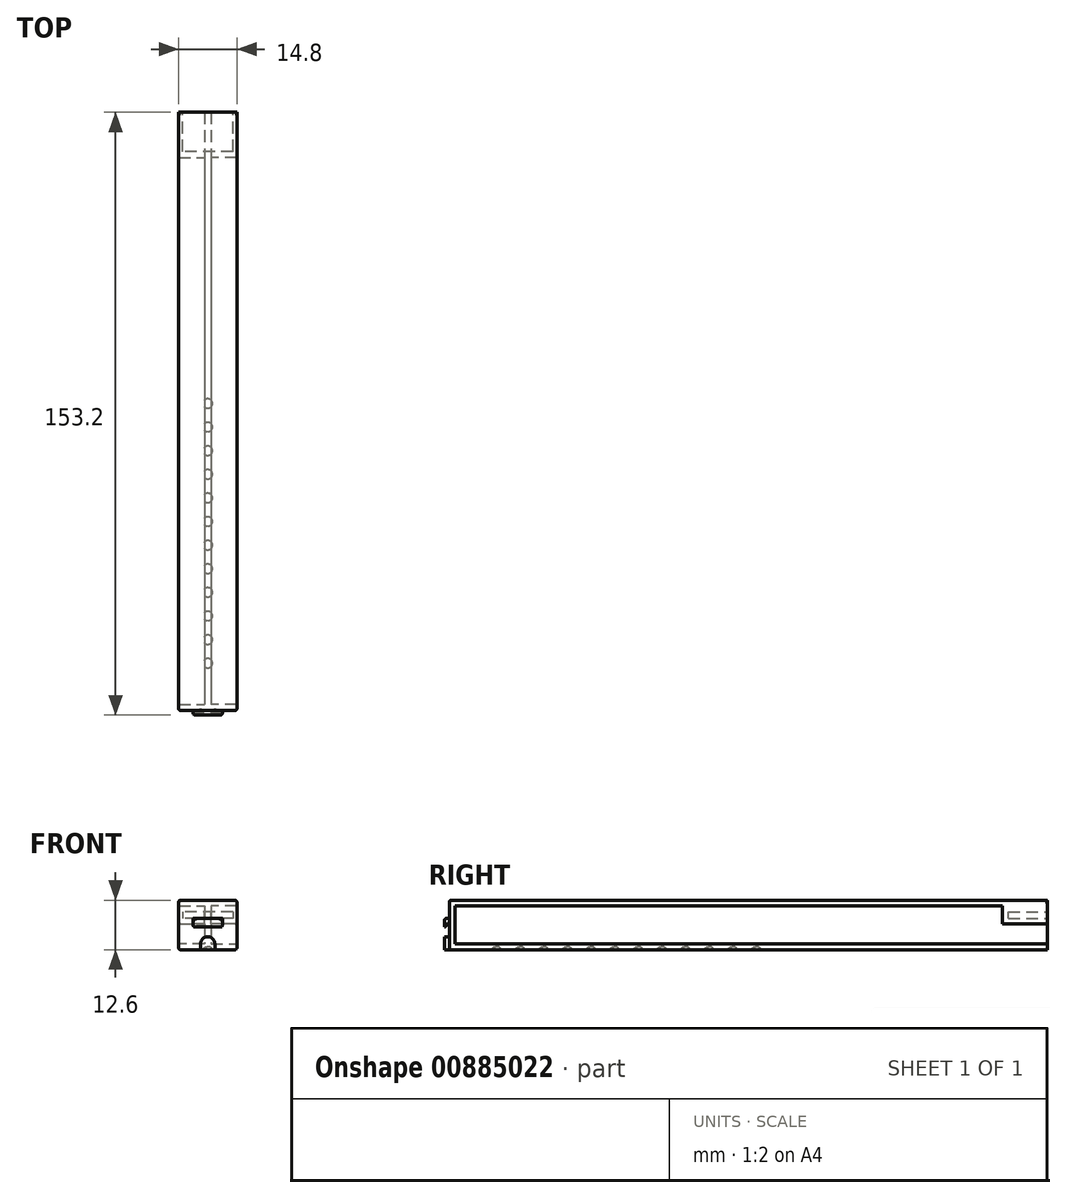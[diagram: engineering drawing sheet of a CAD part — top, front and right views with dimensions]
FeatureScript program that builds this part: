
annotation { "Feature Type Name" : "Feature", "Feature Type Description" : "" }
export const myFeature = defineFeature(function(context is Context, id is Id, definition is map)
    precondition{}
    {
        {
            var Q0;
            Q0=qCreatedBy(makeId("Front.planeOp"),FACE);
            var sketch = newSketch(context, id + "F0", { "sketchPlane" : qUnion([Q0])});
            skLineSegment(sketch, "E0", {"start": v(0, 0) * mm, "end": v(7.4, 0) * mm});
            skLineSegment(sketch, "E1", {"start": v(7.4, 0) * mm, "end": v(7.4, 12.6) * mm, "construction": true});
            skLineSegment(sketch, "E2", {"start": v(7.4, 12.6) * mm, "end": v(0, 12.6) * mm});
            skLineSegment(sketch, "E3", {"start": v(0, 12.6) * mm, "end": v(0, 11.1) * mm});
            skLineSegment(sketch, "E4", {"start": v(0, 11.1) * mm, "end": v(6.6, 11.1) * mm});
            skLineSegment(sketch, "E5", {"start": v(6.6, 11.1) * mm, "end": v(6.6, 1.5) * mm});
            skLineSegment(sketch, "E6", {"start": v(6.6, 1.5) * mm, "end": v(0, 1.5) * mm});
            skLineSegment(sketch, "E7", {"start": v(0, 1.5) * mm, "end": v(0, 0) * mm});
            skLineSegment(sketch, "E8.MirrorCS", {"start": v(7.4, 12.6) * mm, "end": v(14.8, 12.6) * mm});
            skLineSegment(sketch, "E9.MirrorCS", {"start": v(14.8, 12.6) * mm, "end": v(14.8, 11.1) * mm});
            skLineSegment(sketch, "E10.MirrorCS", {"start": v(14.8, 11.1) * mm, "end": v(8.2, 11.1) * mm});
            skLineSegment(sketch, "E11.MirrorCS", {"start": v(8.2, 11.1) * mm, "end": v(8.2, 1.5) * mm});
            skLineSegment(sketch, "E12.MirrorCS", {"start": v(8.2, 1.5) * mm, "end": v(14.8, 1.5) * mm});
            skLineSegment(sketch, "E13.MirrorCS", {"start": v(14.8, 1.5) * mm, "end": v(14.8, 0) * mm});
            skLineSegment(sketch, "E14.MirrorCS", {"start": v(14.8, 0) * mm, "end": v(7.4, 0) * mm});
            skSolve(sketch);
        }
        {
            var Q0;
            Q0=makeQuery(id+"F0.imprint","IMPRINT",FACE,{"disambiguationData":[TD([[makeQuery(id+"F0.imprint","IMPRINT",EDGE,{"derivedFrom":sQuery(id+"F0.wireOp",EDGE,"E0")}),1.0]])]});
            extrude(context, id + "F1", {"entities" : qUnion([Q0]), "oppositeDirection" : true, "depth" : 152 * mm, "offsetDistance" : 25 * mm});
        }
        {
            var Q0;
            Q0=makeQuery(id+"F1.opExtrude","SWEPT_FACE",FACE,{"disambiguationData":[OSD([sQuery(id+"F0.wireOp",EDGE,"E11.MirrorCS")])]});
            var sketch = newSketch(context, id + "F2", { "sketchPlane" : qUnion([Q0])});
            skLineSegment(sketch, "E15.bottom", {"start": v(0, 11.1) * mm, "end": v(1.5, 11.1) * mm});
            skLineSegment(sketch, "E15.top", {"start": v(0, 1.5) * mm, "end": v(1.5, 1.5) * mm});
            skLineSegment(sketch, "E15.left", {"start": v(0, 11.1) * mm, "end": v(0, 1.5) * mm});
            skLineSegment(sketch, "E15.right", {"start": v(1.5, 11.1) * mm, "end": v(1.5, 1.5) * mm});
            skSolve(sketch);
        }
        {
            var Q0;
            Q0=makeQuery(id+"F2.imprint","IMPRINT",FACE,{"disambiguationData":[TD([[makeQuery(id+"F2.imprint","IMPRINT",EDGE,{"derivedFrom":sQuery(id+"F2.wireOp",EDGE,"E15.bottom")}),1.0]])]});
            var Q1;
            Q1=makeQuery(id+"F1.opExtrude","SWEPT_FACE",FACE,{"disambiguationData":[OSD([sQuery(id+"F0.wireOp",EDGE,"E9.MirrorCS")])]});
            extrude(context, id + "F3", {"entities" : qUnion([Q0]), "operationType" : NewBodyOperationType.ADD, "endBound" : BoundingType.UP_TO_SURFACE, "depth" : 25 * mm, "endBoundEntityFace" : qUnion([Q1]), "offsetDistance" : 25 * mm});
        }
        {
            var Q0;
            Q0=makeQuery(id+"F1.opExtrude","SWEPT_FACE",FACE,{"disambiguationData":[OSD([sQuery(id+"F0.wireOp",EDGE,"E5")])]});
            var sketch = newSketch(context, id + "F4", { "sketchPlane" : qUnion([Q0])});
            skLineSegment(sketch, "E16.0", {"start": v(-1.5, 11.1) * mm, "end": v(-1.5, 1.5) * mm});
            skSolve(sketch);
        }
        {
            var Q0;
            {var subQ0=sQuery(id+"F4.wireOp",EDGE,"E16.0");Q0=makeQuery(id+"F4.imprint","IMPRINT",FACE,{"disambiguationData":[TD([[makeQuery(id+"F4.imprint","IMPRINT",EDGE,{"derivedFrom":subQ0}),1.0]])]});}
            var Q1;
            Q1=makeQuery(id+"F1.opExtrude","SWEPT_FACE",FACE,{"disambiguationData":[OSD([sQuery(id+"F0.wireOp",EDGE,"E3")])]});
            extrude(context, id + "F5", {"entities" : qUnion([Q0]), "operationType" : NewBodyOperationType.ADD, "endBound" : BoundingType.UP_TO_SURFACE, "depth" : 25 * mm, "endBoundEntityFace" : qUnion([Q1]), "offsetDistance" : 25 * mm});
        }
        {
            var Q0;
            {var subQ0=sQuery(id+"F0.wireOp",EDGE,"E5");Q0=makeQuery(id+"F5.boolean.opBoolean","MERGE",FACE,{"derivedFrom":[makeQuery(id+"F3.boolean.opBoolean","MERGE",FACE,{"derivedFrom":[makeQuery(id+"F1.opExtrude","CAP_FACE",FACE,{"disambiguationData":[OSD([sQuery(id+"F0.wireOp",EDGE,"E0"),sQuery(id+"F0.wireOp",EDGE,"E2"),sQuery(id+"F0.wireOp",EDGE,"E3"),sQuery(id+"F0.wireOp",EDGE,"E4"),subQ0,sQuery(id+"F0.wireOp",EDGE,"E6"),sQuery(id+"F0.wireOp",EDGE,"E7"),sQuery(id+"F0.wireOp",EDGE,"E8.MirrorCS"),sQuery(id+"F0.wireOp",EDGE,"E9.MirrorCS"),sQuery(id+"F0.wireOp",EDGE,"E10.MirrorCS"),sQuery(id+"F0.wireOp",EDGE,"E11.MirrorCS"),sQuery(id+"F0.wireOp",EDGE,"E12.MirrorCS"),sQuery(id+"F0.wireOp",EDGE,"E13.MirrorCS"),sQuery(id+"F0.wireOp",EDGE,"E14.MirrorCS")])],"isStart":true}),makeQuery(id+"F3.opExtrude","SWEPT_FACE",FACE,{"disambiguationData":[OSD([sQuery(id+"F2.wireOp",EDGE,"E15.left")])]})]}),makeQuery(id+"F5.opExtrude","SWEPT_FACE",FACE,{"disambiguationData":[OSD([subQ0])]})]});}
            var sketch = newSketch(context, id + "F6", { "sketchPlane" : qUnion([Q0])});
            skLineSegment(sketch, "E17.bottom", {"start": v(5.6, 0) * mm, "end": v(9.2, 0) * mm});
            skLineSegment(sketch, "E17.top", {"start": v(7.4, 3.3) * mm, "end": v(7.4, 3.3) * mm});
            skLineSegment(sketch, "E17.left", {"start": v(5.6, 0) * mm, "end": v(5.6, 1.5) * mm});
            skLineSegment(sketch, "E17.right", {"start": v(9.2, 0) * mm, "end": v(9.2, 1.5) * mm});
            skPoint(sketch, "E18.visualSharp", {"position": v(5.6, 3.3) * mm});
            skArc(sketch, "E18.filletArc", {"start": v(7.4, 3.3) * mm, "mid": v(6.13, 2.77) * mm, "end": v(5.6, 1.5) * mm});
            skPoint(sketch, "E19.visualSharp", {"position": v(9.2, 3.3) * mm});
            skArc(sketch, "E19.filletArc", {"start": v(9.2, 1.5) * mm, "mid": v(8.67, 2.77) * mm, "end": v(7.4, 3.3) * mm});
            skLineSegment(sketch, "E20.bottom", {"start": v(3.7, 7.96) * mm, "end": v(11.1, 7.96) * mm});
            skLineSegment(sketch, "E20.top", {"start": v(3.7, 6.66) * mm, "end": v(11.1, 6.66) * mm});
            skLineSegment(sketch, "E20.left", {"start": v(3.7, 7.96) * mm, "end": v(3.7, 6.66) * mm});
            skLineSegment(sketch, "E20.right", {"start": v(11.1, 7.96) * mm, "end": v(11.1, 6.66) * mm});
            skSolve(sketch);
        }
        {
            var Q0;
            Q0=makeQuery(id+"F6.imprint","IMPRINT",FACE,{"disambiguationData":[TD([[makeQuery(id+"F6.imprint","IMPRINT",EDGE,{"derivedFrom":sQuery(id+"F6.wireOp",EDGE,"E17.bottom")}),1.0]])]});
            var Q1;
            Q1=makeQuery(id+"F6.imprint","IMPRINT",FACE,{"disambiguationData":[TD([[makeQuery(id+"F6.imprint","IMPRINT",EDGE,{"derivedFrom":sQuery(id+"F6.wireOp",EDGE,"E20.bottom")}),-1.0]])]});
            extrude(context, id + "F7", {"entities" : qUnion([Q0, Q1]), "operationType" : NewBodyOperationType.ADD, "depth" : 1.2 * mm, "offsetDistance" : 25 * mm});
        }
        {
            var Q0;
            Q0=makeQuery(id+"F7.opExtrude","SWEPT_FACE",FACE,{"disambiguationData":[OSD([sQuery(id+"F6.wireOp",EDGE,"E20.left")])]});
            var sketch = newSketch(context, id + "F8", { "sketchPlane" : qUnion([Q0])});
            skLineSegment(sketch, "E21", {"start": v(1.2, 6.66) * mm, "end": v(1.2, 5.86) * mm});
            skLineSegment(sketch, "E22", {"start": v(1.2, 5.86) * mm, "end": v(0.96, 5.86) * mm});
            skLineSegment(sketch, "E23", {"start": v(0.96, 5.86) * mm, "end": v(0.5, 6.66) * mm});
            skLineSegment(sketch, "E24", {"start": v(0, 6.66) * mm, "end": v(0.5, 6.66) * mm});
            skSolve(sketch);
        }
        {
            var Q0;
            {var subQ0=sQuery(id+"F8.wireOp",EDGE,"E21");Q0=makeQuery(id+"F8.imprint","IMPRINT",FACE,{"disambiguationData":[TD([[makeQuery(id+"F8.imprint","IMPRINT",EDGE,{"derivedFrom":subQ0}),-1.0]])]});}
            var Q1;
            Q1=makeQuery(id+"F7.opExtrude","SWEPT_FACE",FACE,{"disambiguationData":[OSD([sQuery(id+"F6.wireOp",EDGE,"E20.right")])]});
            extrude(context, id + "F9", {"entities" : qUnion([Q0]), "operationType" : NewBodyOperationType.ADD, "endBound" : BoundingType.UP_TO_SURFACE, "oppositeDirection" : true, "depth" : 25 * mm, "endBoundEntityFace" : qUnion([Q1]), "offsetDistance" : 25 * mm});
        }
        {
            var Q0;
            Q0=makeQuery(id+"F1.opExtrude","SWEPT_FACE",FACE,{"disambiguationData":[OSD([sQuery(id+"F0.wireOp",EDGE,"E11.MirrorCS")])]});
            var sketch = newSketch(context, id + "F10", { "sketchPlane" : qUnion([Q0])});
            skLineSegment(sketch, "E25", {"start": v(142, 8.01) * mm, "end": v(152, 8.01) * mm});
            skLineSegment(sketch, "E26", {"start": v(152, 8.01) * mm, "end": v(152, 6.51) * mm});
            skLineSegment(sketch, "E27", {"start": v(152, 6.51) * mm, "end": v(140.5, 6.51) * mm});
            skLineSegment(sketch, "E28", {"start": v(140.5, 6.51) * mm, "end": v(140.5, 11.1) * mm});
            skLineSegment(sketch, "E29", {"start": v(140.5, 11.1) * mm, "end": v(152, 11.1) * mm});
            skLineSegment(sketch, "E30", {"start": v(152, 11.1) * mm, "end": v(152, 9.6) * mm});
            skLineSegment(sketch, "E31", {"start": v(152, 9.6) * mm, "end": v(142, 9.6) * mm});
            skLineSegment(sketch, "E32", {"start": v(142, 9.6) * mm, "end": v(142, 8.01) * mm});
            skSolve(sketch);
        }
        {
            var Q0;
            Q0 = qSketchRegion(id + "FgvDUQmByhWsIWp_1", true);
            var Q1;
            Q1=makeQuery(id+"F10.imprint","IMPRINT",FACE,{"disambiguationData":[TD([[makeQuery(id+"F10.imprint","IMPRINT",EDGE,{"derivedFrom":sQuery(id+"F10.wireOp",EDGE,"E25")}),-1.0]])]});
            var Q2;
            Q2=makeQuery(id+"F3.boolean.opBoolean","MERGE",FACE,{"derivedFrom":[makeQuery(id+"F1.opExtrude","SWEPT_FACE",FACE,{"disambiguationData":[OSD([sQuery(id+"F0.wireOp",EDGE,"E9.MirrorCS")])]}),makeQuery(id+"F1.opExtrude","SWEPT_FACE",FACE,{"disambiguationData":[OSD([sQuery(id+"F0.wireOp",EDGE,"E13.MirrorCS")])]}),makeQuery(id+"F3.opExtrude","CAP_FACE",FACE,{"disambiguationData":[OSD([sQuery(id+"F2.wireOp",EDGE,"E15.bottom"),sQuery(id+"F2.wireOp",EDGE,"E15.top"),sQuery(id+"F2.wireOp",EDGE,"E15.left"),sQuery(id+"F2.wireOp",EDGE,"E15.right")])],"isStart":false})]});
            extrude(context, id + "F11", {"entities" : qUnion([Q0, Q1]), "operationType" : NewBodyOperationType.ADD, "endBound" : BoundingType.UP_TO_SURFACE, "depth" : 25 * mm, "endBoundEntityFace" : qUnion([Q2]), "offsetDistance" : 25 * mm});
        }
        {
            var Q0;
            Q0=makeQuery(id+"F1.opExtrude","SWEPT_FACE",FACE,{"disambiguationData":[OSD([sQuery(id+"F0.wireOp",EDGE,"E5")])]});
            var sketch = newSketch(context, id + "F12", { "sketchPlane" : qUnion([Q0])});
            skLineSegment(sketch, "E33.0", {"start": v(-140.5, 11.1) * mm, "end": v(-152, 11.1) * mm});
            skLineSegment(sketch, "E33.1", {"start": v(-140.5, 6.51) * mm, "end": v(-140.5, 11.1) * mm});
            skLineSegment(sketch, "E33.2", {"start": v(-152, 9.6) * mm, "end": v(-142, 9.6) * mm});
            skLineSegment(sketch, "E33.3", {"start": v(-142, 9.6) * mm, "end": v(-142, 8.01) * mm});
            skLineSegment(sketch, "E33.4", {"start": v(-142, 8.01) * mm, "end": v(-152, 8.01) * mm});
            skLineSegment(sketch, "E33.5", {"start": v(-152, 6.51) * mm, "end": v(-140.5, 6.51) * mm});
            skLineSegment(sketch, "E33.6", {"start": v(-152, 11.1) * mm, "end": v(-152, 9.6) * mm});
            skLineSegment(sketch, "E33.7", {"start": v(-152, 8.01) * mm, "end": v(-152, 6.51) * mm});
            skSolve(sketch);
        }
        {
            var Q0;
            Q0=makeQuery(id+"F12.imprint","IMPRINT",FACE,{"disambiguationData":[TD([[makeQuery(id+"F12.imprint","IMPRINT",EDGE,{"derivedFrom":sQuery(id+"F12.wireOp",EDGE,"E33.0")}),-1.0]])]});
            var Q1;
            Q1=makeQuery(id+"F5.boolean.opBoolean","MERGE",FACE,{"derivedFrom":[makeQuery(id+"F1.opExtrude","SWEPT_FACE",FACE,{"disambiguationData":[OSD([sQuery(id+"F0.wireOp",EDGE,"E3")])]}),makeQuery(id+"F1.opExtrude","SWEPT_FACE",FACE,{"disambiguationData":[OSD([sQuery(id+"F0.wireOp",EDGE,"E7")])]}),makeQuery(id+"F5.opExtrude","CAP_FACE",FACE,{"disambiguationData":[OSD([sQuery(id+"F0.wireOp",EDGE,"E4"),sQuery(id+"F0.wireOp",EDGE,"E5"),sQuery(id+"F0.wireOp",EDGE,"E6"),sQuery(id+"F4.wireOp",EDGE,"E16.0")])],"isStart":false})]});
            extrude(context, id + "F13", {"entities" : qUnion([Q0]), "operationType" : NewBodyOperationType.ADD, "endBound" : BoundingType.UP_TO_SURFACE, "depth" : 25 * mm, "endBoundEntityFace" : qUnion([Q1]), "offsetDistance" : 25 * mm});
        }
        {
            var Q0;
            {var subQ0=sQuery(id+"F0.wireOp",EDGE,"E5");Q0=makeQuery(id+"F13.boolean.opBoolean","MERGE",FACE,{"derivedFrom":[makeQuery(id+"F11.boolean.opBoolean","MERGE",FACE,{"derivedFrom":[makeQuery(id+"F1.opExtrude","CAP_FACE",FACE,{"disambiguationData":[OSD([sQuery(id+"F0.wireOp",EDGE,"E0"),sQuery(id+"F0.wireOp",EDGE,"E2"),sQuery(id+"F0.wireOp",EDGE,"E3"),sQuery(id+"F0.wireOp",EDGE,"E4"),subQ0,sQuery(id+"F0.wireOp",EDGE,"E6"),sQuery(id+"F0.wireOp",EDGE,"E7"),sQuery(id+"F0.wireOp",EDGE,"E8.MirrorCS"),sQuery(id+"F0.wireOp",EDGE,"E9.MirrorCS"),sQuery(id+"F0.wireOp",EDGE,"E10.MirrorCS"),sQuery(id+"F0.wireOp",EDGE,"E11.MirrorCS"),sQuery(id+"F0.wireOp",EDGE,"E12.MirrorCS"),sQuery(id+"F0.wireOp",EDGE,"E13.MirrorCS"),sQuery(id+"F0.wireOp",EDGE,"E14.MirrorCS")])],"isStart":false}),makeQuery(id+"F11.opExtrude","SWEPT_FACE",FACE,{"disambiguationData":[OSD([sQuery(id+"F10.wireOp",EDGE,"E26")])]})]}),makeQuery(id+"F13.opExtrude","SWEPT_FACE",FACE,{"disambiguationData":[OSD([subQ0])]})]});}
            var sketch = newSketch(context, id + "F14", { "sketchPlane" : qUnion([Q0])});
            skLineSegment(sketch, "E34.bottom", {"start": v(-14.8, 9.6) * mm, "end": v(-13.8, 9.6) * mm});
            skLineSegment(sketch, "E34.top", {"start": v(-14.8, 8.01) * mm, "end": v(-13.8, 8.01) * mm});
            skLineSegment(sketch, "E34.left", {"start": v(-14.8, 9.6) * mm, "end": v(-14.8, 8.01) * mm});
            skLineSegment(sketch, "E34.right", {"start": v(-13.8, 9.6) * mm, "end": v(-13.8, 8.01) * mm});
            skLineSegment(sketch, "E35.bottom", {"start": v(0, 9.6) * mm, "end": v(-1, 9.6) * mm});
            skLineSegment(sketch, "E35.top", {"start": v(0, 8.01) * mm, "end": v(-1, 8.01) * mm});
            skLineSegment(sketch, "E35.left", {"start": v(0, 9.6) * mm, "end": v(0, 8.01) * mm});
            skLineSegment(sketch, "E35.right", {"start": v(-1, 9.6) * mm, "end": v(-1, 8.01) * mm});
            skLineSegment(sketch, "E36.bottom", {"start": v(-6.6, 9.6) * mm, "end": v(-8.2, 9.6) * mm});
            skLineSegment(sketch, "E36.top", {"start": v(-6.6, 8.01) * mm, "end": v(-8.2, 8.01) * mm});
            skLineSegment(sketch, "E36.left", {"start": v(-6.6, 9.6) * mm, "end": v(-6.6, 8.01) * mm});
            skLineSegment(sketch, "E36.right", {"start": v(-8.2, 9.6) * mm, "end": v(-8.2, 8.01) * mm});
            skSolve(sketch);
        }
        {
            var Q0;
            Q0=makeQuery(id+"F14.imprint","IMPRINT",FACE,{"disambiguationData":[TD([[makeQuery(id+"F14.imprint","IMPRINT",EDGE,{"derivedFrom":sQuery(id+"F14.wireOp",EDGE,"E34.bottom")}),-1.0]])]});
            var Q1;
            Q1=makeQuery(id+"F14.imprint","IMPRINT",FACE,{"disambiguationData":[TD([[makeQuery(id+"F14.imprint","IMPRINT",EDGE,{"derivedFrom":sQuery(id+"F14.wireOp",EDGE,"E35.bottom")}),1.0]])]});
            extrude(context, id + "F15", {"entities" : qUnion([Q0, Q1]), "operationType" : NewBodyOperationType.ADD, "endBound" : BoundingType.UP_TO_NEXT, "oppositeDirection" : true, "depth" : 25 * mm, "offsetDistance" : 25 * mm});
        }
        {
            var Q0;
            Q0=makeQuery(id+"F14.imprint","IMPRINT",FACE,{"disambiguationData":[TD([[makeQuery(id+"F14.imprint","IMPRINT",EDGE,{"derivedFrom":sQuery(id+"F14.wireOp",EDGE,"E36.bottom")}),1.0]])]});
            var Q1;
            Q1=makeQuery(id+"F13.opExtrude","SWEPT_FACE",FACE,{"disambiguationData":[OSD([sQuery(id+"F12.wireOp",EDGE,"E33.3")])]});
            extrude(context, id + "F16", {"entities" : qUnion([Q0]), "operationType" : NewBodyOperationType.REMOVE, "endBound" : BoundingType.UP_TO_SURFACE, "oppositeDirection" : true, "depth" : 25 * mm, "endBoundEntityFace" : qUnion([Q1]), "offsetDistance" : 25 * mm});
        }
        {
            var Q0;
            Q0=makeQuery(id+"F7.boolean.opBoolean","MERGE",FACE,{"derivedFrom":[makeQuery(id+"F1.opExtrude","SWEPT_FACE",FACE,{"disambiguationData":[OSD([sQuery(id+"F0.wireOp",EDGE,"E0"),sQuery(id+"F0.wireOp",EDGE,"E14.MirrorCS")])]}),makeQuery(id+"F7.opExtrude","SWEPT_FACE",FACE,{"disambiguationData":[OSD([sQuery(id+"F6.wireOp",EDGE,"E17.bottom")])]})]});
            var sketch = newSketch(context, id + "F17", { "sketchPlane" : qUnion([Q0])});
            skCircle(sketch, "E37", {"center": v(7.4, -12) * mm, "radius": 1.2 * mm});
            skLineSegment(sketch, "E38", {"start": v(0, 0) * mm, "end": v(14.8, 0) * mm, "construction": true});
            skLineSegment(sketch, "E39", {"start": v(7.4, -12) * mm, "end": v(7.4, 0) * mm, "construction": true});
            skCircle(sketch, "E40.0.1.0", {"center": v(7.4, -18) * mm, "radius": 1.2 * mm});
            skCircle(sketch, "E40.0.2.0", {"center": v(7.4, -24) * mm, "radius": 1.2 * mm});
            skCircle(sketch, "E40.0.3.0", {"center": v(7.4, -30) * mm, "radius": 1.2 * mm});
            skCircle(sketch, "E40.0.4.0", {"center": v(7.4, -36) * mm, "radius": 1.2 * mm});
            skCircle(sketch, "E40.0.5.0", {"center": v(7.4, -42) * mm, "radius": 1.2 * mm});
            skCircle(sketch, "E40.0.6.0", {"center": v(7.4, -48) * mm, "radius": 1.2 * mm});
            skCircle(sketch, "E40.0.7.0", {"center": v(7.4, -54) * mm, "radius": 1.2 * mm});
            skCircle(sketch, "E40.0.8.0", {"center": v(7.4, -60) * mm, "radius": 1.2 * mm});
            skCircle(sketch, "E40.0.9.0", {"center": v(7.4, -66) * mm, "radius": 1.2 * mm});
            skCircle(sketch, "E40.0.10.0", {"center": v(7.4, -72) * mm, "radius": 1.2 * mm});
            skCircle(sketch, "E40.0.11.0", {"center": v(7.4, -78) * mm, "radius": 1.2 * mm});
            skLineSegment(sketch, "E40.direction1", {"start": v(7.4, -12) * mm, "end": v(31, -12) * mm, "construction": true});
            skLineSegment(sketch, "E40.direction2", {"start": v(7.4, -12) * mm, "end": v(7.4, -18) * mm, "construction": true});
            skSolve(sketch);
        }
        {
            var Q0;
            Q0=makeQuery(id+"F17.imprint","IMPRINT",FACE,{"disambiguationData":[TD([[makeQuery(id+"F17.imprint","IMPRINT",EDGE,{"derivedFrom":sQuery(id+"F17.wireOp",EDGE,"E37")}),1.0]])]});
            var Q1;
            Q1=makeQuery(id+"F17.imprint","IMPRINT",FACE,{"disambiguationData":[TD([[makeQuery(id+"F17.imprint","IMPRINT",EDGE,{"derivedFrom":sQuery(id+"F17.wireOp",EDGE,"E40.0.1.0")}),1.0]])]});
            var Q2;
            Q2=makeQuery(id+"F17.imprint","IMPRINT",FACE,{"disambiguationData":[TD([[makeQuery(id+"F17.imprint","IMPRINT",EDGE,{"derivedFrom":sQuery(id+"F17.wireOp",EDGE,"E40.0.2.0")}),1.0]])]});
            var Q3;
            Q3=makeQuery(id+"F17.imprint","IMPRINT",FACE,{"disambiguationData":[TD([[makeQuery(id+"F17.imprint","IMPRINT",EDGE,{"derivedFrom":sQuery(id+"F17.wireOp",EDGE,"E40.0.3.0")}),1.0]])]});
            var Q4;
            Q4=makeQuery(id+"F17.imprint","IMPRINT",FACE,{"disambiguationData":[TD([[makeQuery(id+"F17.imprint","IMPRINT",EDGE,{"derivedFrom":sQuery(id+"F17.wireOp",EDGE,"E40.0.4.0")}),1.0]])]});
            var Q5;
            Q5=makeQuery(id+"F17.imprint","IMPRINT",FACE,{"disambiguationData":[TD([[makeQuery(id+"F17.imprint","IMPRINT",EDGE,{"derivedFrom":sQuery(id+"F17.wireOp",EDGE,"E40.0.5.0")}),1.0]])]});
            var Q6;
            Q6=makeQuery(id+"F17.imprint","IMPRINT",FACE,{"disambiguationData":[TD([[makeQuery(id+"F17.imprint","IMPRINT",EDGE,{"derivedFrom":sQuery(id+"F17.wireOp",EDGE,"E40.0.6.0")}),1.0]])]});
            var Q7;
            Q7=makeQuery(id+"F17.imprint","IMPRINT",FACE,{"disambiguationData":[TD([[makeQuery(id+"F17.imprint","IMPRINT",EDGE,{"derivedFrom":sQuery(id+"F17.wireOp",EDGE,"E40.0.7.0")}),1.0]])]});
            var Q8;
            Q8=makeQuery(id+"F17.imprint","IMPRINT",FACE,{"disambiguationData":[TD([[makeQuery(id+"F17.imprint","IMPRINT",EDGE,{"derivedFrom":sQuery(id+"F17.wireOp",EDGE,"E40.0.8.0")}),1.0]])]});
            var Q9;
            Q9=makeQuery(id+"F17.imprint","IMPRINT",FACE,{"disambiguationData":[TD([[makeQuery(id+"F17.imprint","IMPRINT",EDGE,{"derivedFrom":sQuery(id+"F17.wireOp",EDGE,"E40.0.9.0")}),1.0]])]});
            var Q10;
            Q10=makeQuery(id+"F17.imprint","IMPRINT",FACE,{"disambiguationData":[TD([[makeQuery(id+"F17.imprint","IMPRINT",EDGE,{"derivedFrom":sQuery(id+"F17.wireOp",EDGE,"E40.0.10.0")}),1.0]])]});
            var Q11;
            Q11=makeQuery(id+"F17.imprint","IMPRINT",FACE,{"disambiguationData":[TD([[makeQuery(id+"F17.imprint","IMPRINT",EDGE,{"derivedFrom":sQuery(id+"F17.wireOp",EDGE,"E40.0.11.0")}),1.0]])]});
            extrude(context, id + "F18", {"entities" : qUnion([Q0, Q1, Q2, Q3, Q4, Q5, Q6, Q7, Q8, Q9, Q10, Q11]), "operationType" : NewBodyOperationType.REMOVE, "oppositeDirection" : true, "depth" : 0.8 * mm, "offsetDistance" : 25 * mm});
        }
        {
            var Q0;
            Q0=makeQuery(id+"F18.boolean.opBoolean","COPY",EDGE,{"derivedFrom":makeQuery(id+"F18.opExtrude","CAP_EDGE",EDGE,{"disambiguationData":[OSD([sQuery(id+"F17.wireOp",EDGE,"E40.0.11.0")])],"isStart":false})});
            var Q1;
            Q1=makeQuery(id+"F18.boolean.opBoolean","COPY",EDGE,{"derivedFrom":makeQuery(id+"F18.opExtrude","CAP_EDGE",EDGE,{"disambiguationData":[OSD([sQuery(id+"F17.wireOp",EDGE,"E40.0.10.0")])],"isStart":false})});
            var Q2;
            Q2=makeQuery(id+"F18.boolean.opBoolean","COPY",EDGE,{"derivedFrom":makeQuery(id+"F18.opExtrude","CAP_EDGE",EDGE,{"disambiguationData":[OSD([sQuery(id+"F17.wireOp",EDGE,"E40.0.9.0")])],"isStart":false})});
            var Q3;
            Q3=makeQuery(id+"F18.boolean.opBoolean","COPY",EDGE,{"derivedFrom":makeQuery(id+"F18.opExtrude","CAP_EDGE",EDGE,{"disambiguationData":[OSD([sQuery(id+"F17.wireOp",EDGE,"E40.0.8.0")])],"isStart":false})});
            var Q4;
            Q4=makeQuery(id+"F18.boolean.opBoolean","COPY",EDGE,{"derivedFrom":makeQuery(id+"F18.opExtrude","CAP_EDGE",EDGE,{"disambiguationData":[OSD([sQuery(id+"F17.wireOp",EDGE,"E40.0.7.0")])],"isStart":false})});
            var Q5;
            Q5=makeQuery(id+"F18.boolean.opBoolean","COPY",EDGE,{"derivedFrom":makeQuery(id+"F18.opExtrude","CAP_EDGE",EDGE,{"disambiguationData":[OSD([sQuery(id+"F17.wireOp",EDGE,"E40.0.6.0")])],"isStart":false})});
            var Q6;
            Q6=makeQuery(id+"F18.boolean.opBoolean","COPY",EDGE,{"derivedFrom":makeQuery(id+"F18.opExtrude","CAP_EDGE",EDGE,{"disambiguationData":[OSD([sQuery(id+"F17.wireOp",EDGE,"E40.0.5.0")])],"isStart":false})});
            var Q7;
            Q7=makeQuery(id+"F18.boolean.opBoolean","COPY",EDGE,{"derivedFrom":makeQuery(id+"F18.opExtrude","CAP_EDGE",EDGE,{"disambiguationData":[OSD([sQuery(id+"F17.wireOp",EDGE,"E40.0.4.0")])],"isStart":false})});
            var Q8;
            Q8=makeQuery(id+"F18.boolean.opBoolean","COPY",EDGE,{"derivedFrom":makeQuery(id+"F18.opExtrude","CAP_EDGE",EDGE,{"disambiguationData":[OSD([sQuery(id+"F17.wireOp",EDGE,"E40.0.3.0")])],"isStart":false})});
            var Q9;
            Q9=makeQuery(id+"F18.boolean.opBoolean","COPY",EDGE,{"derivedFrom":makeQuery(id+"F18.opExtrude","CAP_EDGE",EDGE,{"disambiguationData":[OSD([sQuery(id+"F17.wireOp",EDGE,"E40.0.2.0")])],"isStart":false})});
            var Q10;
            Q10=makeQuery(id+"F18.boolean.opBoolean","COPY",EDGE,{"derivedFrom":makeQuery(id+"F18.opExtrude","CAP_EDGE",EDGE,{"disambiguationData":[OSD([sQuery(id+"F17.wireOp",EDGE,"E40.0.1.0")])],"isStart":false})});
            var Q11;
            Q11=makeQuery(id+"F18.boolean.opBoolean","COPY",EDGE,{"derivedFrom":makeQuery(id+"F18.opExtrude","CAP_EDGE",EDGE,{"disambiguationData":[OSD([sQuery(id+"F17.wireOp",EDGE,"E37")])],"isStart":false})});
            fillet(context, id + "F19", {"entities" : qUnion([Q0, Q1, Q2, Q3, Q4, Q5, Q6, Q7, Q8, Q9, Q10, Q11]), "radius" : 1.2 * mm, "tangentPropagation" : true, "allowEdgeOverflow" : false});
        }
        {
            var Q0;
            Q0=makeQuery(id+"F16.boolean.opBoolean","COPY",EDGE,{"derivedFrom":makeQuery(id+"F16.opExtrude","SWEPT_EDGE",EDGE,{"disambiguationData":[OSD([sQuery(id+"F0.wireOp",EDGE,"E2"),sQuery(id+"F0.wireOp",EDGE,"E8.MirrorCS"),sQuery(id+"F14.wireOp",EDGE,"0EWzOAzJ-FitD-dZOc-zAf9-mVBQwacMPEmS"),sQuery(id+"F14.wireOp",EDGE,"3a1VO8J1-pKlq-Oro1-SVKx-ygcU3vKSFJe3")])]})});
            var Q1;
            Q1=makeQuery(id+"F16.boolean.opBoolean","COPY",EDGE,{"derivedFrom":makeQuery(id+"F16.opExtrude","SWEPT_EDGE",EDGE,{"disambiguationData":[OSD([sQuery(id+"F0.wireOp",EDGE,"E10.MirrorCS"),sQuery(id+"F14.wireOp",EDGE,"0EWzOAzJ-FitD-dZOc-zAf9-mVBQwacMPEmS"),sQuery(id+"F14.wireOp",EDGE,"chC3mlCo-7ysk-qYXu-zDaA-1en8GhesRIkC")])]})});
            var Q2;
            Q2=makeQuery(id+"F16.boolean.opBoolean","COPY",EDGE,{"derivedFrom":makeQuery(id+"F16.opExtrude","SWEPT_EDGE",EDGE,{"disambiguationData":[OSD([sQuery(id+"F0.wireOp",EDGE,"E2"),sQuery(id+"F0.wireOp",EDGE,"E8.MirrorCS"),sQuery(id+"F14.wireOp",EDGE,"ceRFCyRu-8BYw-4e90-c2ns-8t8g8dATU1da"),sQuery(id+"F14.wireOp",EDGE,"3a1VO8J1-pKlq-Oro1-SVKx-ygcU3vKSFJe3")])]})});
            var Q3;
            Q3=makeQuery(id+"F16.boolean.opBoolean","COPY",EDGE,{"derivedFrom":makeQuery(id+"F16.opExtrude","SWEPT_EDGE",EDGE,{"disambiguationData":[OSD([sQuery(id+"F0.wireOp",EDGE,"E4"),sQuery(id+"F14.wireOp",EDGE,"va9mFEuU-5wCR-oyVD-Y4VQ-zi8C2ubbxEkB"),sQuery(id+"F14.wireOp",EDGE,"ceRFCyRu-8BYw-4e90-c2ns-8t8g8dATU1da")])]})});
            var Q4;
            Q4=makeQuery(id+"F16.boolean.opBoolean","COPY",EDGE,{"derivedFrom":makeQuery(id+"F16.opExtrude","CAP_EDGE",EDGE,{"disambiguationData":[OSD([sQuery(id+"F14.wireOp",EDGE,"0EWzOAzJ-FitD-dZOc-zAf9-mVBQwacMPEmS")])],"isStart":true})});
            var Q5;
            Q5=makeQuery(id+"F16.boolean.opBoolean","COPY",EDGE,{"derivedFrom":makeQuery(id+"F16.opExtrude","CAP_EDGE",EDGE,{"disambiguationData":[OSD([sQuery(id+"F14.wireOp",EDGE,"ceRFCyRu-8BYw-4e90-c2ns-8t8g8dATU1da")])],"isStart":true})});
            var Q6;
            Q6=makeQuery(id+"F1.opExtrude","CAP_EDGE",EDGE,{"disambiguationData":[OSD([sQuery(id+"F0.wireOp",EDGE,"E10.MirrorCS")])],"isStart":false});
            var Q7;
            Q7=makeQuery(id+"F15.opExtrude","CAP_EDGE",EDGE,{"disambiguationData":[OSD([sQuery(id+"F14.wireOp",EDGE,"407AdA0n-u7l6-K8e3-t0Ld-mCcvsT80spbc.right")])],"isStart":true});
            var Q8;
            Q8=makeQuery(id+"F16.boolean.opBoolean","MERGE",EDGE,{"derivedFrom":[makeQuery(id+"F11.opExtrude","SWEPT_EDGE",EDGE,{"disambiguationData":[OSD([sQuery(id+"F10.wireOp",EDGE,"E25"),sQuery(id+"F10.wireOp",EDGE,"E26"),sQuery(id+"F10.wireOp",EDGE,"vd0n2bWI-2w59-8aZA-U7OC-NVR1PWX096RI")])]}),makeQuery(id+"F13.opExtrude","SWEPT_EDGE",EDGE,{"disambiguationData":[OSD([sQuery(id+"F0.wireOp",EDGE,"E5"),sQuery(id+"FgvDUQmByhWsIWp_1.wireOp",EDGE,"494ee2e7-549b-4880-af38-ae2305f98c9e.0")])]})],"fromTools":[makeQuery(id+"F16.opExtrude","CAP_EDGE",EDGE,{"disambiguationData":[OSD([sQuery(id+"F14.wireOp",EDGE,"XO4pMfx4-b2yW-cmLo-uSqd-TG0deKBsu0AE")])],"isStart":true})]});
            var Q9;
            Q9=makeQuery(id+"F15.opExtrude","CAP_EDGE",EDGE,{"disambiguationData":[OSD([sQuery(id+"F14.wireOp",EDGE,"t20VARuM-3wV1-ago3-HXmc-T0NwQvSHDK2S.right")])],"isStart":true});
            var Q10;
            Q10=makeQuery(id+"F1.opExtrude","CAP_EDGE",EDGE,{"disambiguationData":[OSD([sQuery(id+"F0.wireOp",EDGE,"E4")])],"isStart":false});
            var Q11;
            {var subQ3=sQuery(id+"F0.wireOp",EDGE,"E8.MirrorCS");var subQ6=sQuery(id+"F0.wireOp",EDGE,"E3");var subQ7=sQuery(id+"F0.wireOp",EDGE,"E2");Q11=makeQuery(id+"F16.boolean.opBoolean","SPLIT",EDGE,{"disambiguationData":[TD([makeQuery(id+"F1.opExtrude","SWEPT_FACE",FACE,{"disambiguationData":[OSD([subQ6])]})])],"derivedFrom":makeQuery(id+"F1.opExtrude","CAP_EDGE",EDGE,{"disambiguationData":[OSD([subQ7,subQ3])],"isStart":false})});}
            var Q12;
            {var subQ4=sQuery(id+"F0.wireOp",EDGE,"E9.MirrorCS");var subQ5=sQuery(id+"F0.wireOp",EDGE,"E8.MirrorCS");var subQ6=sQuery(id+"F0.wireOp",EDGE,"E2");Q12=makeQuery(id+"F16.boolean.opBoolean","SPLIT",EDGE,{"disambiguationData":[TD([makeQuery(id+"F1.opExtrude","SWEPT_FACE",FACE,{"disambiguationData":[OSD([subQ4])]})])],"derivedFrom":makeQuery(id+"F1.opExtrude","CAP_EDGE",EDGE,{"disambiguationData":[OSD([subQ6,subQ5])],"isStart":false})});}
            fillet(context, id + "F20", {"entities" : qUnion([Q0, Q1, Q2, Q3, Q4, Q5, Q6, Q7, Q8, Q9, Q10, Q11, Q12]), "radius" : 0.3 * mm, "tangentPropagation" : true, "allowEdgeOverflow" : false});
        }
        {
            var Q0;
            Q0=makeQuery(id+"F3.boolean.opBoolean","MERGE",EDGE,{"derivedFrom":[makeQuery(id+"F1.opExtrude","CAP_EDGE",EDGE,{"disambiguationData":[OSD([sQuery(id+"F0.wireOp",EDGE,"E9.MirrorCS")])],"isStart":true}),makeQuery(id+"F1.opExtrude","CAP_EDGE",EDGE,{"disambiguationData":[OSD([sQuery(id+"F0.wireOp",EDGE,"E13.MirrorCS")])],"isStart":true}),makeQuery(id+"F3.opExtrude","CAP_EDGE",EDGE,{"disambiguationData":[OSD([sQuery(id+"F2.wireOp",EDGE,"E15.left")])],"isStart":false})]});
            var Q1;
            Q1=makeQuery(id+"F1.opExtrude","CAP_EDGE",EDGE,{"disambiguationData":[OSD([sQuery(id+"F0.wireOp",EDGE,"E2"),sQuery(id+"F0.wireOp",EDGE,"E8.MirrorCS")])],"isStart":true});
            var Q2;
            Q2=makeQuery(id+"F5.boolean.opBoolean","MERGE",EDGE,{"derivedFrom":[makeQuery(id+"F1.opExtrude","CAP_EDGE",EDGE,{"disambiguationData":[OSD([sQuery(id+"F0.wireOp",EDGE,"E3")])],"isStart":true}),makeQuery(id+"F1.opExtrude","CAP_EDGE",EDGE,{"disambiguationData":[OSD([sQuery(id+"F0.wireOp",EDGE,"E7")])],"isStart":true}),makeQuery(id+"F5.opExtrude","CAP_EDGE",EDGE,{"disambiguationData":[OSD([sQuery(id+"F0.wireOp",EDGE,"E5")])],"isStart":false})]});
            var Q3;
            {var subQ1=sQuery(id+"F0.wireOp",EDGE,"E14.MirrorCS");var subQ2=sQuery(id+"F0.wireOp",EDGE,"E0");var subQ3=sQuery(id+"F0.wireOp",EDGE,"E9.MirrorCS");Q3=makeQuery(id+"F7.boolean.opBoolean","SPLIT",EDGE,{"disambiguationData":[TD([makeQuery(id+"F1.opExtrude","SWEPT_FACE",FACE,{"disambiguationData":[OSD([subQ3])]})])],"derivedFrom":makeQuery(id+"F1.opExtrude","CAP_EDGE",EDGE,{"disambiguationData":[OSD([subQ2,subQ1])],"isStart":true})});}
            var Q4;
            {var subQ1=sQuery(id+"F0.wireOp",EDGE,"E3");var subQ2=sQuery(id+"F0.wireOp",EDGE,"E14.MirrorCS");var subQ3=sQuery(id+"F0.wireOp",EDGE,"E0");Q4=makeQuery(id+"F7.boolean.opBoolean","SPLIT",EDGE,{"disambiguationData":[TD([makeQuery(id+"F1.opExtrude","SWEPT_FACE",FACE,{"disambiguationData":[OSD([subQ1])]})])],"derivedFrom":makeQuery(id+"F1.opExtrude","CAP_EDGE",EDGE,{"disambiguationData":[OSD([subQ3,subQ2])],"isStart":true})});}
            var Q5;
            Q5=makeQuery(id+"F7.opExtrude","CAP_EDGE",EDGE,{"disambiguationData":[OSD([sQuery(id+"F6.wireOp",EDGE,"E20.bottom")])],"isStart":false});
            var Q6;
            Q6=makeQuery(id+"F9.boolean.opBoolean","MERGE",EDGE,{"derivedFrom":[makeQuery(id+"F7.opExtrude","CAP_EDGE",EDGE,{"disambiguationData":[OSD([sQuery(id+"F6.wireOp",EDGE,"E20.right")])],"isStart":false}),makeQuery(id+"F9.opExtrude","CAP_EDGE",EDGE,{"disambiguationData":[OSD([sQuery(id+"F8.wireOp",EDGE,"E21")])],"isStart":false})]});
            var Q7;
            Q7=makeQuery(id+"F9.boolean.opBoolean","MERGE",EDGE,{"derivedFrom":[makeQuery(id+"F7.opExtrude","CAP_EDGE",EDGE,{"disambiguationData":[OSD([sQuery(id+"F6.wireOp",EDGE,"E20.left")])],"isStart":false}),makeQuery(id+"F9.opExtrude","CAP_EDGE",EDGE,{"disambiguationData":[OSD([sQuery(id+"F8.wireOp",EDGE,"E21")])],"isStart":true})]});
            var Q8;
            Q8=makeQuery(id+"F1.opExtrude","SWEPT_EDGE",EDGE,{"disambiguationData":[OSD([sQuery(id+"F0.wireOp",EDGE,"E8.MirrorCS"),sQuery(id+"F0.wireOp",EDGE,"E9.MirrorCS")])]});
            var Q9;
            Q9=makeQuery(id+"F1.opExtrude","SWEPT_EDGE",EDGE,{"disambiguationData":[OSD([sQuery(id+"F0.wireOp",EDGE,"E2"),sQuery(id+"F0.wireOp",EDGE,"E3")])]});
            var Q10;
            Q10=makeQuery(id+"F1.opExtrude","SWEPT_EDGE",EDGE,{"disambiguationData":[OSD([sQuery(id+"F0.wireOp",EDGE,"E13.MirrorCS"),sQuery(id+"F0.wireOp",EDGE,"E14.MirrorCS")])]});
            var Q11;
            Q11=makeQuery(id+"F1.opExtrude","SWEPT_EDGE",EDGE,{"disambiguationData":[OSD([sQuery(id+"F0.wireOp",EDGE,"E0"),sQuery(id+"F0.wireOp",EDGE,"E7")])]});
            fillet(context, id + "F21", {"entities" : qUnion([Q0, Q1, Q2, Q3, Q4, Q5, Q6, Q7, Q8, Q9, Q10, Q11]), "radius" : 0.5 * mm, "tangentPropagation" : true, "allowEdgeOverflow" : false});
        }
    });
